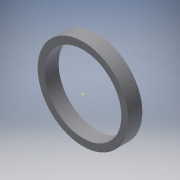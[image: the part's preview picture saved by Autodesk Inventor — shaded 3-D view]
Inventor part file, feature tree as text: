
AUTODESK INVENTOR PART (.ipt)
format: ipt  version: 2019 (Build 230136000, 136)  size: 105,472 bytes
history: native  units: in
note: dims shown in document units (in); Inventor stores cm internally (conversion verified against a paired STEP export)
features: sketch x2, extrude x1
ambient origin geometry x8: Origin, YZ Plane, XZ Plane, XY Plane, X Axis, Y Axis, Z Axis, Center Point
bodies: Solid1 (feature_tree)
feature tree (3):
  extrude  "Extrusion1"  Depth=0.65in
  sketch  "Sketch2"  dims[d2=0.1in d3=0.0in]
  sketch  "Sketch1"  dims[d0=0.55in d1=0.65in]
